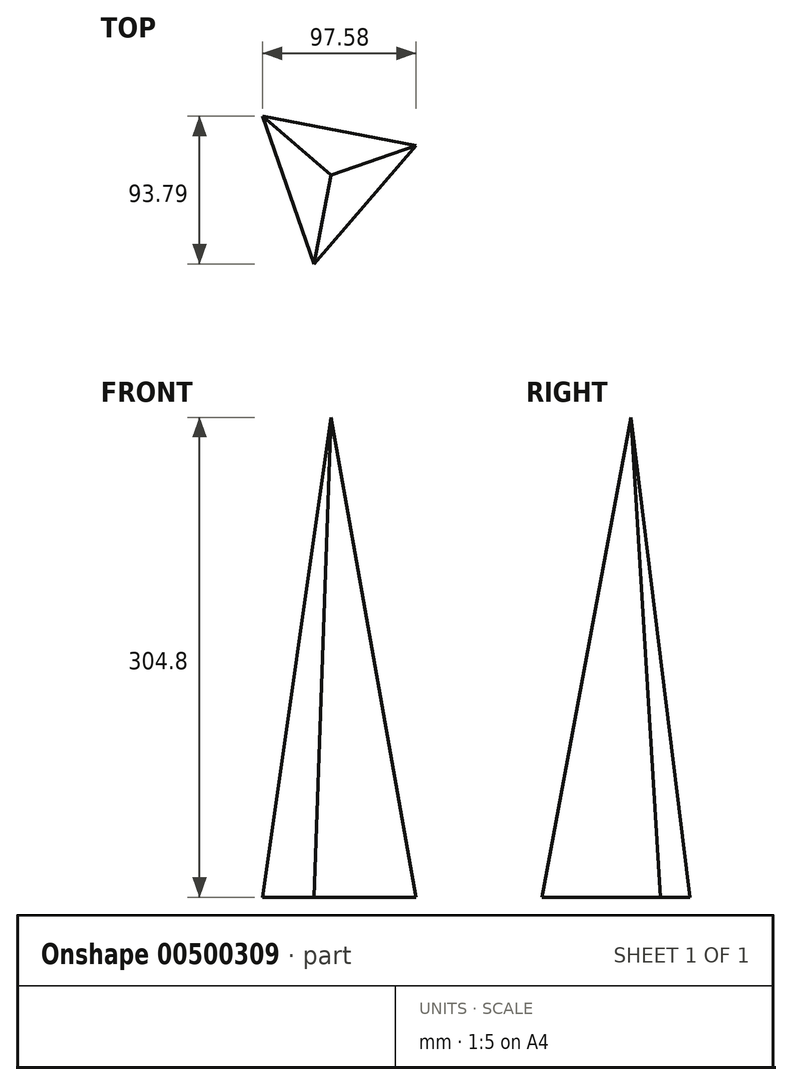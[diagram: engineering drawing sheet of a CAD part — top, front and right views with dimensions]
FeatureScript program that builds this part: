
annotation { "Feature Type Name" : "Feature", "Feature Type Description" : "" }
export const myFeature = defineFeature(function(context is Context, id is Id, definition is map)
    precondition{}
    {
        {
            var Q0;
            Q0=qCreatedBy(makeId("Top.planeOp"),FACE);
            var sketch = newSketch(context, id + "F0", { "sketchPlane" : qUnion([Q0])});
            skCircle(sketch, "E0.cCircle", {"center": v(0, 0) * mm, "radius": 57.35 * mm, "construction": true});
            skLineSegment(sketch, "E0.0", {"start": v(-43.43, 37.45) * mm, "end": v(54.15, 18.88) * mm});
            skLineSegment(sketch, "E0.1", {"start": v(54.15, 18.88) * mm, "end": v(-10.72, -56.34) * mm});
            skLineSegment(sketch, "E0.2", {"start": v(-10.72, -56.34) * mm, "end": v(-43.43, 37.45) * mm});
            skSolve(sketch);
        }
        {
            var Q0;
            Q0=qCreatedBy(makeId("Top.planeOp"),FACE);
            cPlane(context, id + "F1", {"entities" : qUnion([Q0]), "cplaneType" : CPlaneType.OFFSET, "offset" : 304.8 * mm, "width" : 152.4 * mm, "height" : 152.4 * mm});
        }
        {
            var Q0;
            Q0=qCreatedBy(id+"F1.planeOp",FACE);
            var sketch = newSketch(context, id + "F2", { "sketchPlane" : qUnion([Q0])});
            skPoint(sketch, "E1", {"position": v(0, 0) * mm});
            skSolve(sketch);
        }
        {
            var Q0;
            Q0=sQuery(id+"F2.wireOp",VERTEX,"E1");
            var Q1;
            Q1=makeQuery(id+"F0.imprint","IMPRINT",FACE,{"disambiguationData":[TD([[makeQuery(id+"F0.imprint","IMPRINT",EDGE,{"derivedFrom":sQuery(id+"F0.wireOp",EDGE,"E0.0")}),-1.0]])]});
            loft(context, id + "F3", {"sheetProfilesArray" : [{ "sheetProfileEntities" : qUnion([Q0]) }, { "sheetProfileEntities" : qUnion([Q1]) }]});
        }
    });
